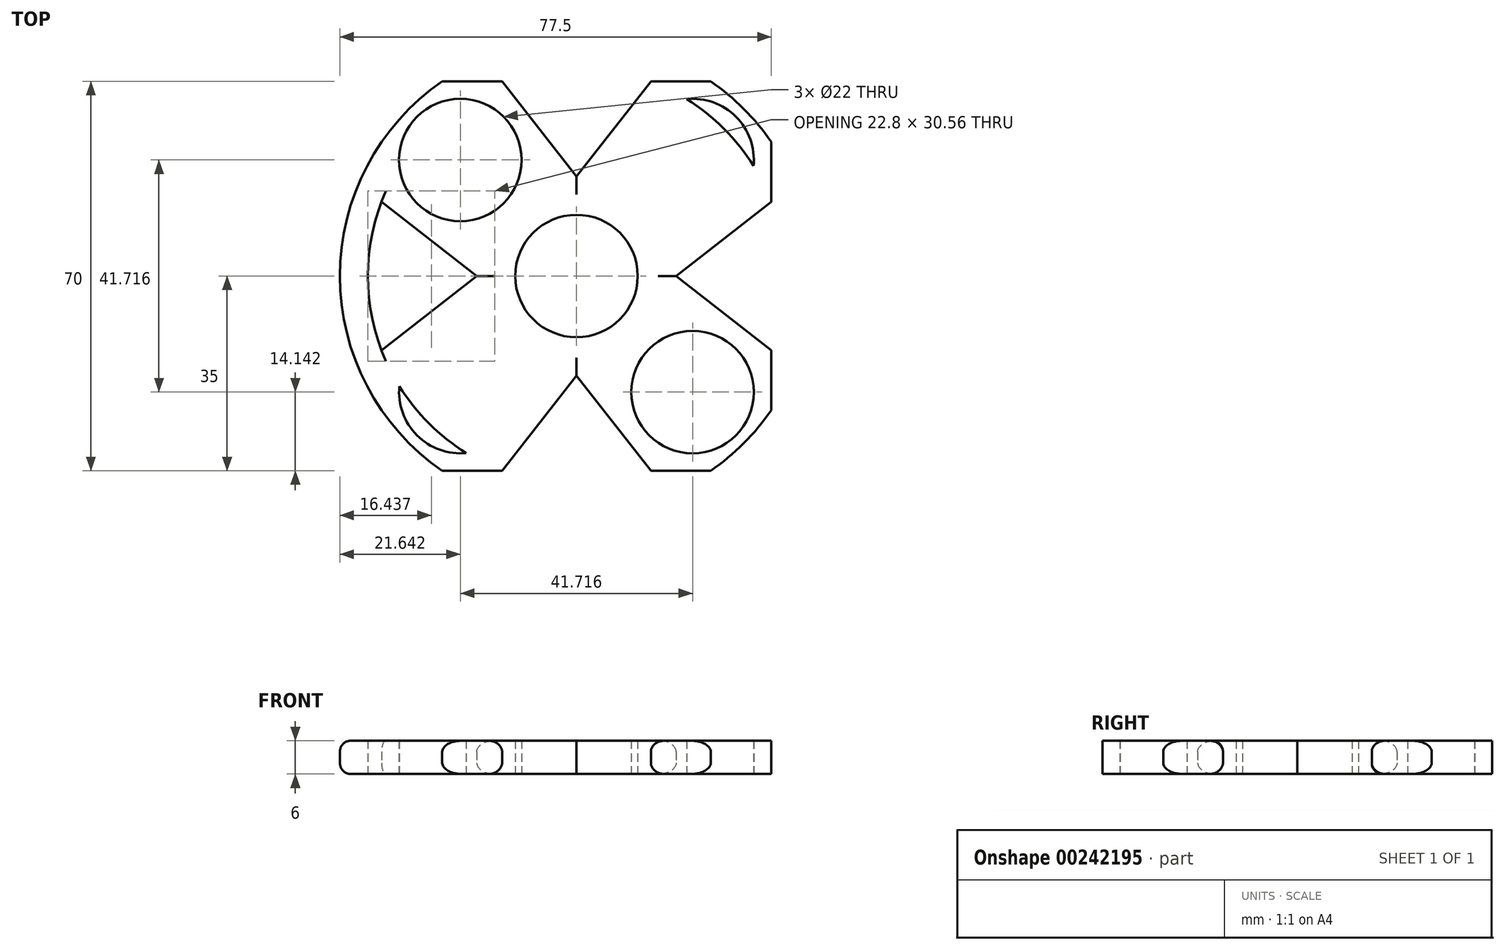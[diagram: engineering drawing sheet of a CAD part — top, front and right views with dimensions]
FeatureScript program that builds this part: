
annotation { "Feature Type Name" : "Feature", "Feature Type Description" : "" }
export const myFeature = defineFeature(function(context is Context, id is Id, definition is map)
    precondition{}
    {
        {
            var Q0;
            Q0=qCreatedBy(makeId("Top.planeOp"),FACE);
            var sketch = newSketch(context, id + "F0", { "sketchPlane" : qUnion([Q0])});
            skLineSegment(sketch, "E0.bottom", {"start": v(35, -35) * mm, "end": v(-35, -35) * mm});
            skLineSegment(sketch, "E0.top", {"start": v(35, 35) * mm, "end": v(-35, 35) * mm});
            skLineSegment(sketch, "E0.left", {"start": v(35, -35) * mm, "end": v(35, 35) * mm});
            skLineSegment(sketch, "E0.right", {"start": v(-35, -35) * mm, "end": v(-35, 35) * mm});
            skPoint(sketch, "E0.middle", {"position": v(0, 0) * mm});
            skCircle(sketch, "E1", {"center": v(0, 0) * mm, "radius": 11 * mm});
            skLineSegment(sketch, "E2", {"start": v(-35, 35) * mm, "end": v(35, -35) * mm, "construction": true});
            skCircle(sketch, "E3", {"center": v(-20.86, 20.86) * mm, "radius": 11 * mm});
            skCircle(sketch, "E4.MirrorC", {"center": v(20.86, 20.86) * mm, "radius": 11 * mm});
            skCircle(sketch, "E5.MirrorC", {"center": v(-20.86, -20.86) * mm, "radius": 11 * mm});
            skCircle(sketch, "E6.MirrorC", {"center": v(20.86, -20.86) * mm, "radius": 11 * mm});
            skLineSegment(sketch, "E7", {"start": v(-13.36, 35) * mm, "end": v(0, 17.9) * mm});
            skLineSegment(sketch, "E8.MirrorCS", {"start": v(13.36, 35) * mm, "end": v(0, 17.9) * mm});
            skLineSegment(sketch, "E9.MirrorCS", {"start": v(-13.36, -35) * mm, "end": v(0, -17.9) * mm});
            skLineSegment(sketch, "E10.MirrorCS", {"start": v(13.36, -35) * mm, "end": v(0, -17.9) * mm});
            skLineSegment(sketch, "E11.MirrorCS", {"start": v(-35, 13.36) * mm, "end": v(-17.9, 0) * mm});
            skLineSegment(sketch, "E12.MirrorCS", {"start": v(-35, -13.36) * mm, "end": v(-17.9, 0) * mm});
            skLineSegment(sketch, "E13.MirrorCS", {"start": v(35, 13.36) * mm, "end": v(17.9, 0) * mm});
            skLineSegment(sketch, "E14.MirrorCS", {"start": v(35, -13.36) * mm, "end": v(17.9, 0) * mm});
            skCircle(sketch, "E15", {"center": v(0, 0) * mm, "radius": 42.5 * mm});
            skCircle(sketch, "E16", {"center": v(0, 0) * mm, "radius": 37.46 * mm});
            skSolve(sketch);
        }
        {
            var Q0;
            Q0=makeQuery(id+"F0.imprint","IMPRINT",FACE,{"disambiguationData":[TD([[makeQuery(id+"F0.imprint","IMPRINT",EDGE,{"derivedFrom":sQuery(id+"F0.wireOp",EDGE,"E1")}),-1.0]])]});
            var Q1;
            {var subQ5=sQuery(id+"F0.wireOp",EDGE,"E16");var subQ6=sQuery(id+"F0.wireOp",EDGE,"E3");var subQ7=makeQuery(id+"F0.imprint","INTERSECT",VERTEX,{"disambiguationData":[OD(0.0)],"derivedFrom":[subQ6,subQ5]});Q1=makeQuery(id+"F0.imprint","IMPRINT",FACE,{"disambiguationData":[TD([[makeQuery(id+"F0.imprint","IMPRINT",EDGE,{"disambiguationData":[TD([[subQ7,-1.0]])],"derivedFrom":subQ6}),-1.0]])]});}
            var Q2;
            {var subQ1=sQuery(id+"F0.wireOp",EDGE,"E0.top");var subQ3=sQuery(id+"F0.wireOp",EDGE,"E15");var subQ4=makeQuery(id+"F0.imprint","INTERSECT",VERTEX,{"disambiguationData":[OD(0.0)],"derivedFrom":[subQ1,subQ3]});Q2=makeQuery(id+"F0.imprint","IMPRINT",FACE,{"disambiguationData":[TD([[makeQuery(id+"F0.imprint","IMPRINT",EDGE,{"disambiguationData":[TD([[subQ4,-1.0]])],"derivedFrom":subQ3}),1.0]])]});}
            var Q3;
            {var subQ5=sQuery(id+"F0.wireOp",EDGE,"E16");var subQ6=sQuery(id+"F0.wireOp",EDGE,"E4.MirrorC");var subQ7=makeQuery(id+"F0.imprint","INTERSECT",VERTEX,{"disambiguationData":[OD(0.0)],"derivedFrom":[subQ6,subQ5]});Q3=makeQuery(id+"F0.imprint","IMPRINT",FACE,{"disambiguationData":[TD([[makeQuery(id+"F0.imprint","IMPRINT",EDGE,{"disambiguationData":[TD([[subQ7,1.0]])],"derivedFrom":subQ6}),1.0]])]});}
            var Q4;
            {var subQ1=sQuery(id+"F0.wireOp",EDGE,"E0.left");var subQ3=sQuery(id+"F0.wireOp",EDGE,"E15");var subQ4=makeQuery(id+"F0.imprint","INTERSECT",VERTEX,{"disambiguationData":[OD(0.0)],"derivedFrom":[subQ1,subQ3]});Q4=makeQuery(id+"F0.imprint","IMPRINT",FACE,{"disambiguationData":[TD([[makeQuery(id+"F0.imprint","IMPRINT",EDGE,{"disambiguationData":[TD([[subQ4,-1.0]])],"derivedFrom":subQ3}),1.0]])]});}
            var Q5;
            {var subQ5=sQuery(id+"F0.wireOp",EDGE,"E16");var subQ6=sQuery(id+"F0.wireOp",EDGE,"E6.MirrorC");var subQ7=makeQuery(id+"F0.imprint","INTERSECT",VERTEX,{"disambiguationData":[OD(0.0)],"derivedFrom":[subQ6,subQ5]});Q5=makeQuery(id+"F0.imprint","IMPRINT",FACE,{"disambiguationData":[TD([[makeQuery(id+"F0.imprint","IMPRINT",EDGE,{"disambiguationData":[TD([[subQ7,-1.0]])],"derivedFrom":subQ6}),-1.0]])]});}
            var Q6;
            {var subQ1=sQuery(id+"F0.wireOp",EDGE,"E0.bottom");var subQ3=sQuery(id+"F0.wireOp",EDGE,"E15");var subQ4=makeQuery(id+"F0.imprint","INTERSECT",VERTEX,{"disambiguationData":[OD(0.0)],"derivedFrom":[subQ1,subQ3]});Q6=makeQuery(id+"F0.imprint","IMPRINT",FACE,{"disambiguationData":[TD([[makeQuery(id+"F0.imprint","IMPRINT",EDGE,{"disambiguationData":[TD([[subQ4,1.0]])],"derivedFrom":subQ3}),1.0]])]});}
            var Q7;
            {var subQ0=sQuery(id+"F0.wireOp",EDGE,"E16");var subQ1=sQuery(id+"F0.wireOp",EDGE,"E5.MirrorC");var subQ2=makeQuery(id+"F0.imprint","INTERSECT",VERTEX,{"disambiguationData":[OD(0.0)],"derivedFrom":[subQ1,subQ0]});Q7=makeQuery(id+"F0.imprint","IMPRINT",FACE,{"disambiguationData":[TD([[makeQuery(id+"F0.imprint","IMPRINT",EDGE,{"disambiguationData":[TD([[subQ2,1.0]])],"derivedFrom":subQ1}),1.0]])]});}
            var Q8;
            {var subQ1=sQuery(id+"F0.wireOp",EDGE,"E0.right");var subQ3=sQuery(id+"F0.wireOp",EDGE,"E15");var subQ4=makeQuery(id+"F0.imprint","INTERSECT",VERTEX,{"disambiguationData":[OD(0.0)],"derivedFrom":[subQ1,subQ3]});Q8=makeQuery(id+"F0.imprint","IMPRINT",FACE,{"disambiguationData":[TD([[makeQuery(id+"F0.imprint","IMPRINT",EDGE,{"disambiguationData":[TD([[subQ4,1.0]])],"derivedFrom":subQ3}),1.0]])]});}
            extrude(context, id + "F1", {"entities" : qUnion([Q0, Q1, Q2, Q3, Q4, Q5, Q6, Q7, Q8]), "depth" : 6 * mm, "offsetDistance" : 25 * mm});
        }
        {
            var Q0;
            Q0=makeQuery(id+"F1.opExtrude","CAP_EDGE",EDGE,{"disambiguationData":[OSD([sQuery(id+"F0.wireOp",EDGE,"E15")])],"isStart":false});
            var Q1;
            Q1=makeQuery(id+"F1.opExtrude","CAP_EDGE",EDGE,{"disambiguationData":[OSD([sQuery(id+"F0.wireOp",EDGE,"E15")])],"isStart":true});
            var Q2;
            Q2=makeQuery(id+"F1.opExtrude","CAP_EDGE",EDGE,{"disambiguationData":[OSD([sQuery(id+"F0.wireOp",EDGE,"E11.MirrorCS")])],"isStart":false});
            var Q3;
            Q3=makeQuery(id+"F1.opExtrude","CAP_EDGE",EDGE,{"disambiguationData":[OSD([sQuery(id+"F0.wireOp",EDGE,"E12.MirrorCS")])],"isStart":false});
            var Q4;
            Q4=makeQuery(id+"F1.opExtrude","CAP_EDGE",EDGE,{"disambiguationData":[OSD([sQuery(id+"F0.wireOp",EDGE,"E9.MirrorCS")])],"isStart":false});
            var Q5;
            Q5=makeQuery(id+"F1.opExtrude","CAP_EDGE",EDGE,{"disambiguationData":[OSD([sQuery(id+"F0.wireOp",EDGE,"E10.MirrorCS")])],"isStart":false});
            var Q6;
            Q6=makeQuery(id+"F1.opExtrude","CAP_EDGE",EDGE,{"disambiguationData":[OSD([sQuery(id+"F0.wireOp",EDGE,"E14.MirrorCS")])],"isStart":false});
            var Q7;
            Q7=makeQuery(id+"F1.opExtrude","CAP_EDGE",EDGE,{"disambiguationData":[OSD([sQuery(id+"F0.wireOp",EDGE,"E13.MirrorCS")])],"isStart":false});
            var Q8;
            Q8=makeQuery(id+"F1.opExtrude","CAP_EDGE",EDGE,{"disambiguationData":[OSD([sQuery(id+"F0.wireOp",EDGE,"E8.MirrorCS")])],"isStart":false});
            var Q9;
            Q9=makeQuery(id+"F1.opExtrude","CAP_EDGE",EDGE,{"disambiguationData":[OSD([sQuery(id+"F0.wireOp",EDGE,"E7")])],"isStart":false});
            var Q10;
            Q10=makeQuery(id+"F1.opExtrude","CAP_EDGE",EDGE,{"disambiguationData":[OSD([sQuery(id+"F0.wireOp",EDGE,"E8.MirrorCS")])],"isStart":true});
            var Q11;
            Q11=makeQuery(id+"F1.opExtrude","CAP_EDGE",EDGE,{"disambiguationData":[OSD([sQuery(id+"F0.wireOp",EDGE,"E7")])],"isStart":true});
            var Q12;
            Q12=makeQuery(id+"F1.opExtrude","CAP_EDGE",EDGE,{"disambiguationData":[OSD([sQuery(id+"F0.wireOp",EDGE,"E11.MirrorCS")])],"isStart":true});
            var Q13;
            Q13=makeQuery(id+"F1.opExtrude","CAP_EDGE",EDGE,{"disambiguationData":[OSD([sQuery(id+"F0.wireOp",EDGE,"E12.MirrorCS")])],"isStart":true});
            var Q14;
            Q14=makeQuery(id+"F1.opExtrude","CAP_EDGE",EDGE,{"disambiguationData":[OSD([sQuery(id+"F0.wireOp",EDGE,"E9.MirrorCS")])],"isStart":true});
            var Q15;
            Q15=makeQuery(id+"F1.opExtrude","CAP_EDGE",EDGE,{"disambiguationData":[OSD([sQuery(id+"F0.wireOp",EDGE,"E10.MirrorCS")])],"isStart":true});
            var Q16;
            Q16=makeQuery(id+"F1.opExtrude","CAP_EDGE",EDGE,{"disambiguationData":[OSD([sQuery(id+"F0.wireOp",EDGE,"E14.MirrorCS")])],"isStart":true});
            var Q17;
            Q17=makeQuery(id+"F1.opExtrude","CAP_EDGE",EDGE,{"disambiguationData":[OSD([sQuery(id+"F0.wireOp",EDGE,"E13.MirrorCS")])],"isStart":true});
            fillet(context, id + "F2", {"entities" : qUnion([Q0, Q1, Q2, Q3, Q4, Q5, Q6, Q7, Q8, Q9, Q10, Q11, Q12, Q13, Q14, Q15, Q16, Q17]), "radius" : 2 * mm, "tangentPropagation" : true, "allowEdgeOverflow" : false});
        }
    });
